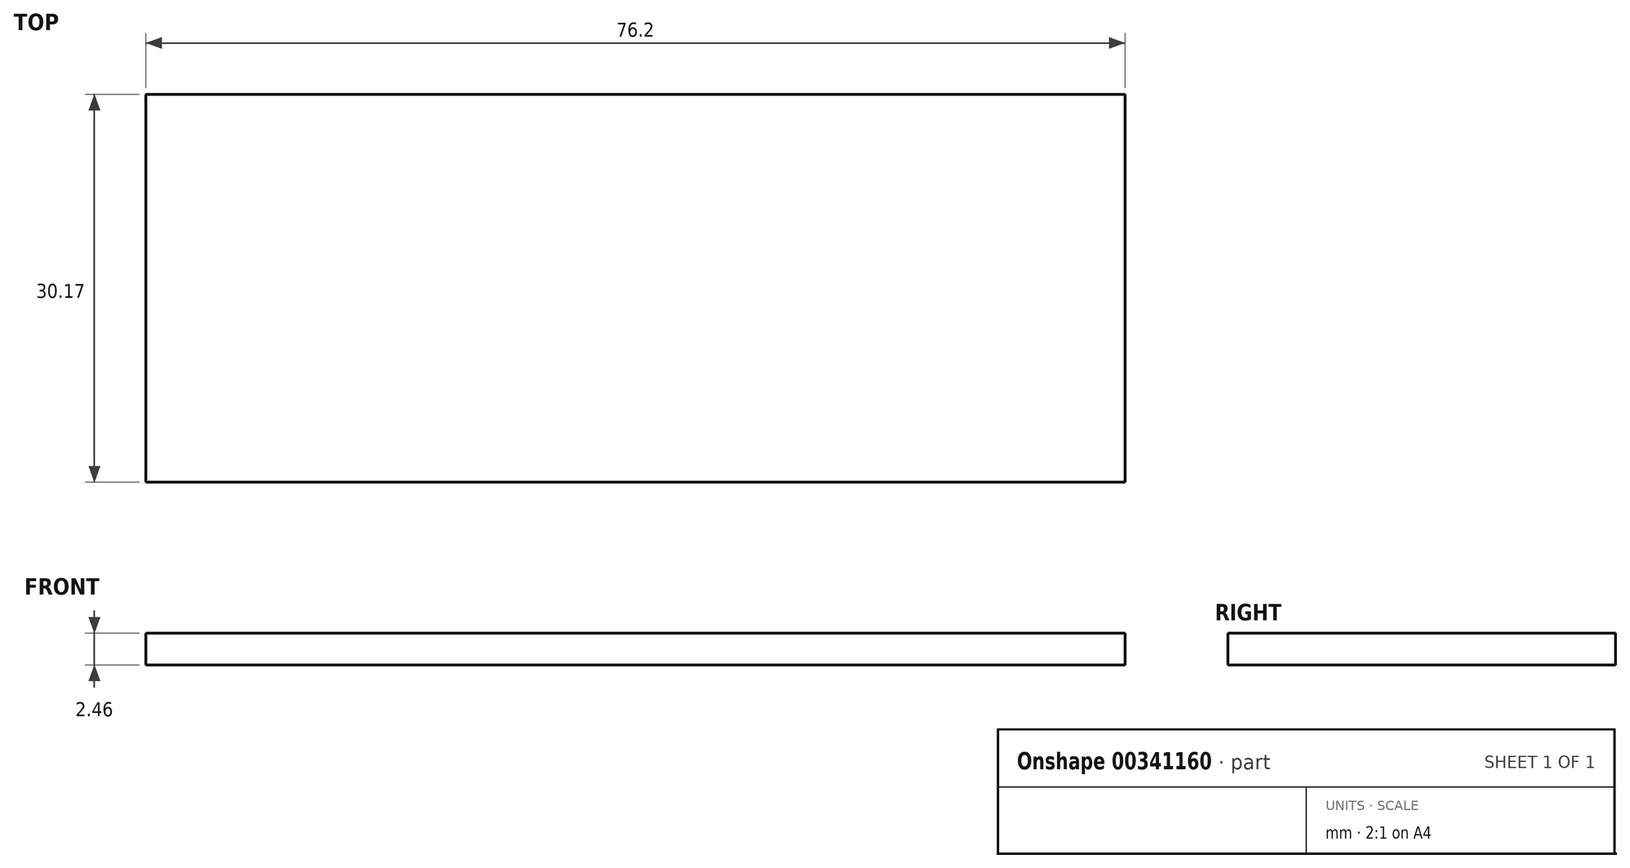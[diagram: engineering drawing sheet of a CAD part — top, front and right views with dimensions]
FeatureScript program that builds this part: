
annotation { "Feature Type Name" : "Feature", "Feature Type Description" : "" }
export const myFeature = defineFeature(function(context is Context, id is Id, definition is map)
    precondition{}
    {
        {
            var Q0;
            Q0=qCreatedBy(makeId("Top.planeOp"),FACE);
            var sketch = newSketch(context, id + "F0", { "sketchPlane" : qUnion([Q0])});
            skLineSegment(sketch, "E0.bottom", {"start": v(54.08, -17.41) * mm, "end": v(-22.12, -17.41) * mm});
            skLineSegment(sketch, "E0.top", {"start": v(54.08, 12.76) * mm, "end": v(-22.12, 12.76) * mm});
            skLineSegment(sketch, "E0.left", {"start": v(54.08, -17.41) * mm, "end": v(54.08, 12.76) * mm});
            skLineSegment(sketch, "E0.right", {"start": v(-22.12, -17.41) * mm, "end": v(-22.12, 12.76) * mm});
            skSolve(sketch);
        }
        {
            var Q0;
            Q0 = qSketchRegion(id + "F0", true);
            extrude(context, id + "F1", {"entities" : qUnion([Q0]), "depth" : 2.46 * mm});
        }
    });
